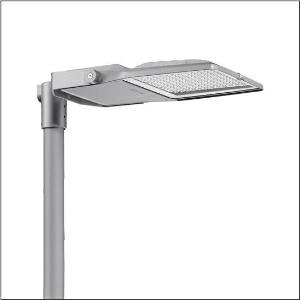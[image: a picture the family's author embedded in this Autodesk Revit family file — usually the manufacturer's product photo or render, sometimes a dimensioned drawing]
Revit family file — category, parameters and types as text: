
# Revit family: floodlight_fl_21_midi___pl52_5xa7785f2d3a_eb33
name_source: partatom
category: Lighting Fixtures
units: mm (PartAtom-declared; Revit-internal decimal feet)

## family parameters
Cut with Voids When Loaded = No
Host = Face
Light Source = No
Part Type = Normal
Room Calculation Point = No
Round Connector Dimension = Use Diameter
Shared = No

## types (1)
- --- (1 x LED, 35750 lm, 271.6 W, 3000K)
    Apparent Load = 272 VA
    CIE Flux Codes = 26 60 98 100 100
    Color Rendering = 70
    Color Temperature = 3000K
    Default Elevation = 1800 mm
    Description = Floodlight FL 21 midi, floodlight, primary light control with lens, of PMMA, primary optical cover: protective disc, of toughened safety glass, transparent, light distribution: PL52, light emission: direct distribution, installation type: surface-mounted, LED, High Power LED, rated luminous flux: 35.750lm, luminous efficacy: 132lm/W, light colour: 730, colour temperature: 3000K, control gear: ECG Smart Interface, control: flexible luminous flux parameterisation, time-dependent luminous flux control, constant luminous flux control, overheat protection, pre-setting: logarithmic dimming characteristic, with terminal, 6-pole, mains connection: 220..240V, AC, 50/60Hz, start of lifetime: 272W, end of service life: 287W, reduction: 123W, luminaire housing, of diecast aluminium, powder-coated, Siteco® metallic grey (DB 702S), sealing non-destructively replaceable, please order mast flange separately, mast bracket, of steel, galvanised, powder-coated, Siteco® metallic grey (DB 702S), Smart Interface above, protection rating (complete): IP66, insulation class (complete): insulation class II (safety insulation), certification: CE, ENEC, VDE, protection symbol: D, impact resistance: IK08, permissible operating ambient temperature: -40..+40°C, permissible operating ambient temperature for outdoor applications: -40..+50°C, standard: DIN EN 12944, LABS conformity tested according to VDMA 24364:2018-05, packaging unit: 1 piece

Light Distribution: PL52
    Height = 76 mm
    Lamp = 1 x LED
    Lamp Light Flux = 35750 lm
    Lamp Power = 271.6 W
    Lamp count = 1
    Length = 657 mm
    Luminous efficacy = 132 lm/W
    Manufacturer = Siteco
    ModVariant = No
    Model = 5XA7785F2D3A
    Number of Poles = 1
    OnlyDefault = Yes
    Power Factor = 1
    Product Name = Floodlight FL 21 midi | PL52
    Product group = floodlight | pylon annexe
    ProductGroupID = 6200
    Protection Class = Protection class II
    Protection Degree = IP 66
    RLX_Detail_Level = 1
    RLX_Emergency_Light_Flux = 0 lm
    RLX_Emergency_Type = 0
    RLX_Emergency_Type_DB = No
    RlxData = <blob elided: 153789 chars, md5=38320d0c>
    Socket = socket
    Standby Power = 0 W
    System Light Flux = 35750 lm
    System Power = 272 W
    Type Comments = factory setting: luminous flux: 100 % | dim-lin: 254 | 620 mA
    Type Image = l_1007123.jpg
    URL = http://relux.com
    VarID = @adj_148763
    Voltage = 0 V
    Weight = 0.00 kg
    Width = 442 mm

## geometry (parser evidence)
native form markers: Blend x4, Sweep x13
no freeform markers — native parametric forms only
